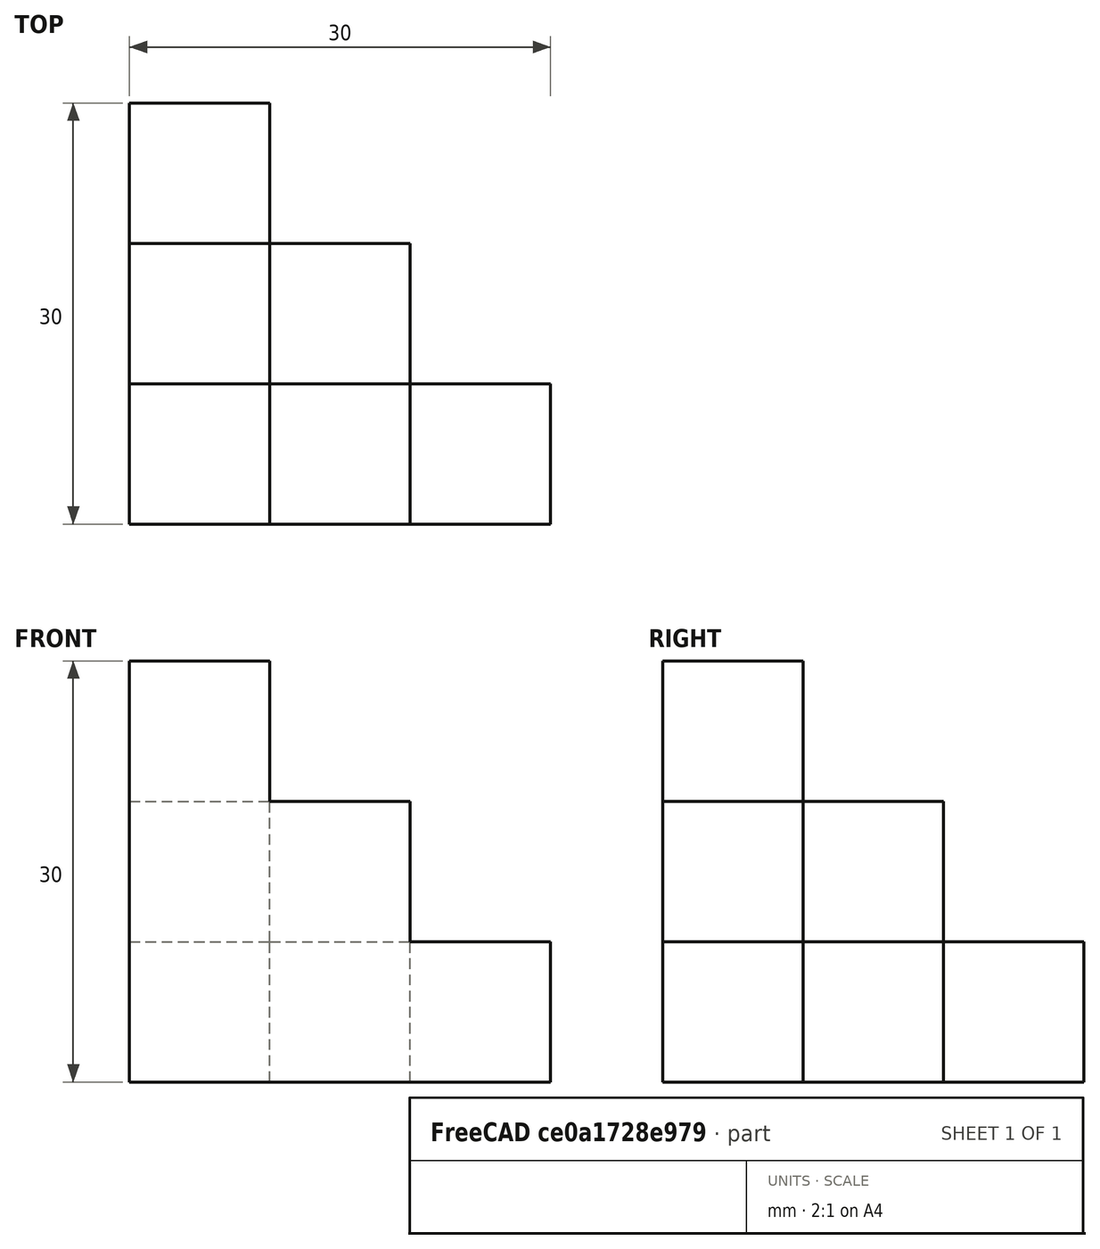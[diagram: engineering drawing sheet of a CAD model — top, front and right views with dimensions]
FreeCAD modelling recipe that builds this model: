
FCSTD DOCUMENT  (FreeCAD 1.0R39319 (Git))
Label: ojt1_t05_r02 refineQbert_3-levels
License: All rights reserved
LicenseURL: https://en.wikipedia.org/wiki/All_rights_reserved
objects: Part::Box×6, Part::MultiFuse×1
note: 7 computed .brp shape members not serialized (recipe doc carries the construction recipe); baked Part::Feature solids carry a one-line shape summary decoded from their .brp

FEATURE [Part::Box] Box  label="Cubo"
  AttacherType = Attacher::AttachEngine3D
  Height = 10
  Length = 30
  Width = 10
FEATURE [Part::Box] Box001  label="Cubo001"
  AttacherType = Attacher::AttachEngine3D
  Height = 10
  Length = 10
  Width = 30
FEATURE [Part::Box] Box002  label="Cubo002"
  AttacherType = Attacher::AttachEngine3D
  Height = 10
  Length = 20
  Width = 20
FEATURE [Part::Box] Box003  label="Cubo003"
  AttacherType = Attacher::AttachEngine3D
  Height = 10
  Length = 20
  Placement = pos=(0,0,10) rot=(0,0,1;0rad)
  Width = 10
FEATURE [Part::Box] Box004  label="Cubo004"
  AttacherType = Attacher::AttachEngine3D
  Height = 10
  Length = 10
  Placement = pos=(0,0,10) rot=(0,0,1;0rad)
  Width = 20
FEATURE [Part::Box] Box005  label="Cubo005"
  AttacherType = Attacher::AttachEngine3D
  Height = 10
  Length = 10
  Placement = pos=(0,0,20) rot=(0,0,1;0rad)
  Width = 10
FEATURE [Part::MultiFuse] Fusion
  Refine = true
  Shapes = -> [Box005,Box,Box001,Box002,Box003,Box004]
